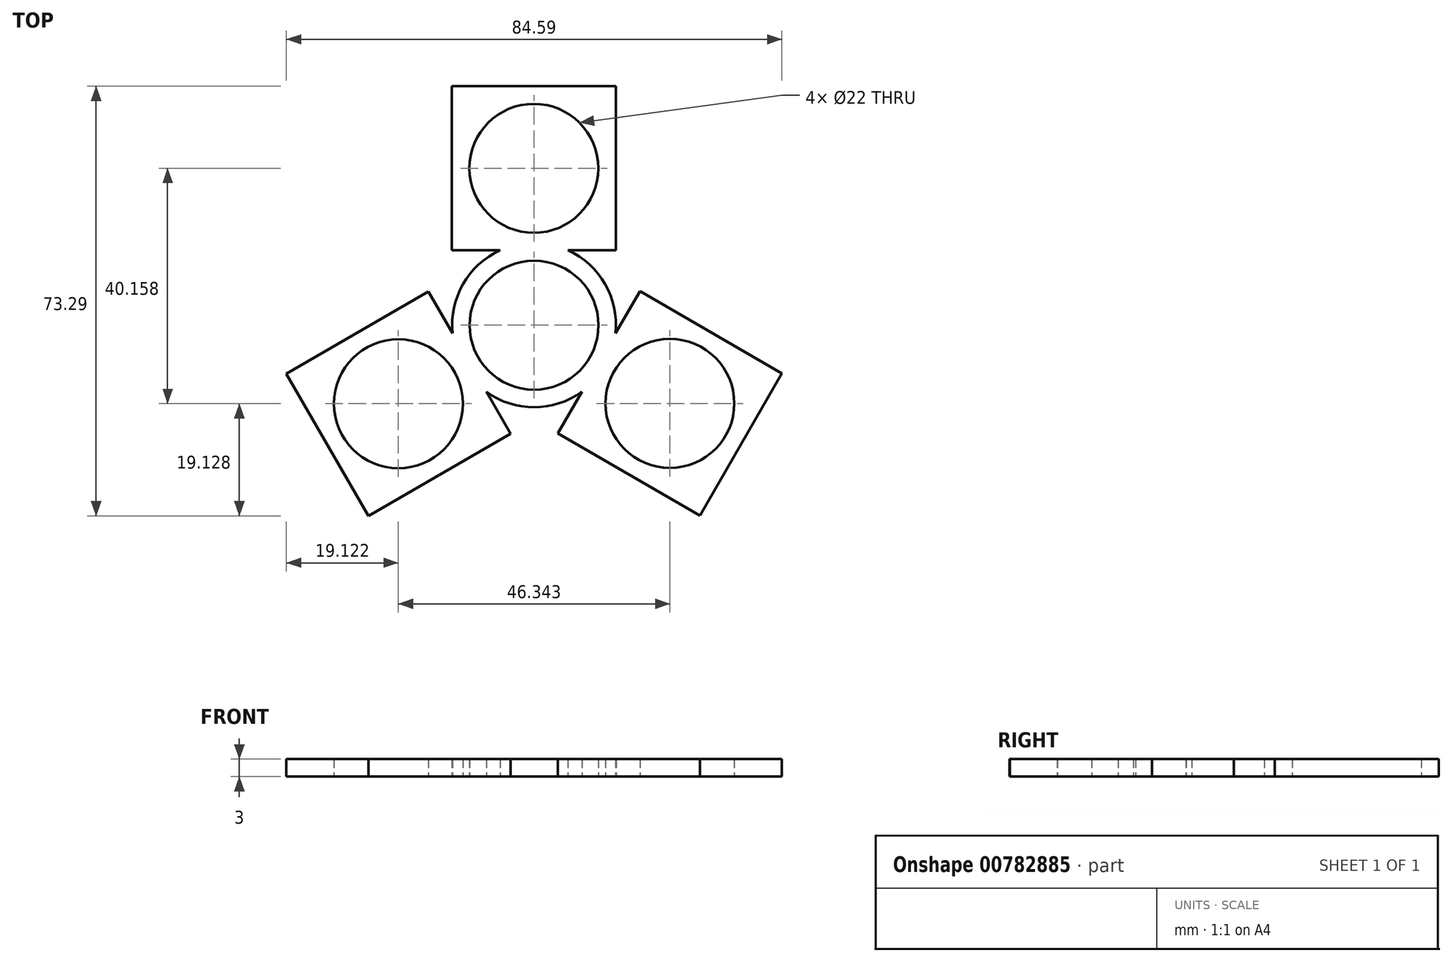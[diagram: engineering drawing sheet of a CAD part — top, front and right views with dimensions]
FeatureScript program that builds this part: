
annotation { "Feature Type Name" : "Feature", "Feature Type Description" : "" }
export const myFeature = defineFeature(function(context is Context, id is Id, definition is map)
    precondition{}
    {
        {
            var Q0;
            Q0=qCreatedBy(makeId("Top.planeOp"),FACE);
            var sketch = newSketch(context, id + "F0", { "sketchPlane" : qUnion([Q0])});
            skArc(sketch, "E0", {"start": v(9.53, 5.5) * mm, "mid": v(0, 11) * mm, "end": v(-9.53, 5.5) * mm});
            skCircle(sketch, "E1", {"center": v(-0.03, 26.76) * mm, "radius": 11 * mm});
            skArc(sketch, "E2", {"start": v(-5.77, 12.76) * mm, "mid": v(-9.4, 10.38) * mm, "end": v(-12.12, 7) * mm});
            skArc(sketch, "E3.trimOffspring", {"start": v(12.12, 7) * mm, "mid": v(9.4, 10.38) * mm, "end": v(5.77, 12.76) * mm});
            skLineSegment(sketch, "E4.bottom", {"start": v(13.97, 12.76) * mm, "end": v(5.77, 12.76) * mm});
            skLineSegment(sketch, "E4.top", {"start": v(13.97, 40.76) * mm, "end": v(-14.03, 40.76) * mm});
            skLineSegment(sketch, "E4.left", {"start": v(13.97, 12.76) * mm, "end": v(13.97, 40.76) * mm});
            skLineSegment(sketch, "E4.right", {"start": v(-14.03, 12.76) * mm, "end": v(-14.03, 40.76) * mm});
            skLineSegment(sketch, "E5.1.0", {"start": v(-18.03, 5.72) * mm, "end": v(-13.93, -1.38) * mm});
            skArc(sketch, "E5.1.1", {"start": v(-12.12, 7) * mm, "mid": v(-13.69, 2.95) * mm, "end": v(-13.93, -1.38) * mm});
            skLineSegment(sketch, "E5.1.3", {"start": v(-18.03, 5.72) * mm, "end": v(-42.28, -8.28) * mm});
            skCircle(sketch, "E5.1.5", {"center": v(-23.16, -13.4) * mm, "radius": 11 * mm});
            skArc(sketch, "E5.1.7", {"start": v(-9.53, 5.5) * mm, "mid": v(-9.53, -5.5) * mm, "end": v(0, -11) * mm});
            skArc(sketch, "E5.1.8", {"start": v(-8.16, -11.37) * mm, "mid": v(-4.29, -13.33) * mm, "end": v(0, -14) * mm});
            skLineSegment(sketch, "E5.1.9", {"start": v(-4.03, -18.53) * mm, "end": v(-28.28, -32.53) * mm});
            skPoint(sketch, "E5.1.10", {"position": v(-23.16, -13.4) * mm});
            skLineSegment(sketch, "E5.1.11", {"start": v(-42.28, -8.28) * mm, "end": v(-28.28, -32.53) * mm});
            skLineSegment(sketch, "E5.2.0", {"start": v(4.06, -18.48) * mm, "end": v(8.16, -11.37) * mm});
            skArc(sketch, "E5.2.1", {"start": v(0, -14) * mm, "mid": v(4.29, -13.33) * mm, "end": v(8.16, -11.37) * mm});
            skLineSegment(sketch, "E5.2.3", {"start": v(4.06, -18.48) * mm, "end": v(28.3, -32.48) * mm});
            skCircle(sketch, "E5.2.5", {"center": v(23.19, -13.35) * mm, "radius": 11 * mm});
            skArc(sketch, "E5.2.7", {"start": v(0, -11) * mm, "mid": v(9.53, -5.5) * mm, "end": v(9.53, 5.5) * mm});
            skArc(sketch, "E5.2.8", {"start": v(13.93, -1.38) * mm, "mid": v(13.69, 2.95) * mm, "end": v(12.12, 7) * mm});
            skLineSegment(sketch, "E5.2.9", {"start": v(18.06, 5.77) * mm, "end": v(42.3, -8.23) * mm});
            skPoint(sketch, "E5.2.10", {"position": v(23.19, -13.35) * mm});
            skLineSegment(sketch, "E5.2.11", {"start": v(28.3, -32.48) * mm, "end": v(42.3, -8.23) * mm});
            skLineSegment(sketch, "E6.trimOffspring", {"start": v(-5.77, 12.76) * mm, "end": v(-14.03, 12.76) * mm});
            skLineSegment(sketch, "E7.trimOffspring", {"start": v(-8.16, -11.37) * mm, "end": v(-4.03, -18.53) * mm});
            skLineSegment(sketch, "E8.trimOffspring", {"start": v(13.93, -1.38) * mm, "end": v(18.06, 5.77) * mm});
            skSolve(sketch);
        }
        {
            var Q0;
            Q0 = qSketchRegion(id + "F0", true);
            extrude(context, id + "F1", {"entities" : qUnion([Q0]), "depth" : 3 * mm, "offsetDistance" : 25 * mm});
        }
    });
